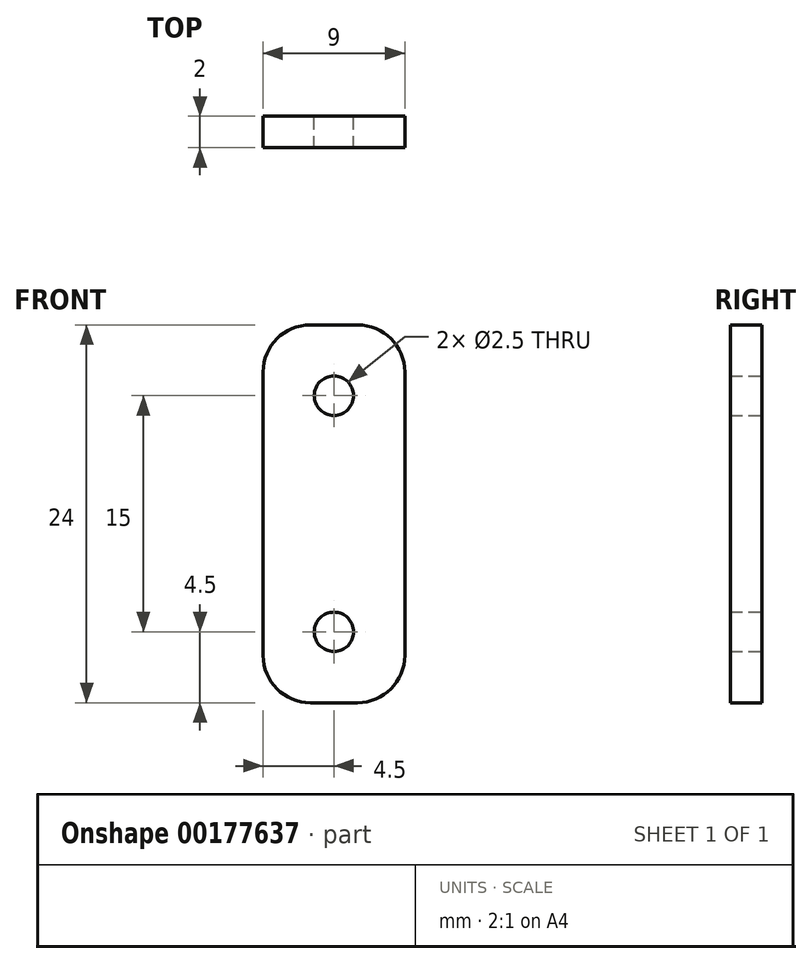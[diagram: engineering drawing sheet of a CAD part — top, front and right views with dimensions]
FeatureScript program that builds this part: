
annotation { "Feature Type Name" : "Feature", "Feature Type Description" : "" }
export const myFeature = defineFeature(function(context is Context, id is Id, definition is map)
    precondition{}
    {
        {
            var Q0;
            Q0=qCreatedBy(makeId("Front.planeOp"),FACE);
            var sketch = newSketch(context, id + "F0", { "sketchPlane" : qUnion([Q0])});
            skLineSegment(sketch, "E0.bottom", {"start": v(4.5, 12) * mm, "end": v(-4.5, 12) * mm});
            skLineSegment(sketch, "E0.top", {"start": v(4.5, -12) * mm, "end": v(-4.5, -12) * mm});
            skLineSegment(sketch, "E0.left", {"start": v(4.5, 12) * mm, "end": v(4.5, -12) * mm});
            skLineSegment(sketch, "E0.right", {"start": v(-4.5, 12) * mm, "end": v(-4.5, -12) * mm});
            skPoint(sketch, "E0.middle", {"position": v(0, 0) * mm});
            skCircle(sketch, "E1", {"center": v(0, 7.5) * mm, "radius": 1.25 * mm});
            skCircle(sketch, "E2", {"center": v(0, -7.5) * mm, "radius": 1.25 * mm});
            skSolve(sketch);
        }
        {
            var Q0;
            Q0=qSketchRegion(id+"F0",true);
            extrude(context, id + "F1", {"entities" : qUnion([Q0]), "depth" : 2 * mm});
        }
        {
            var Q0;
            Q0=makeQuery(id+"F1.opExtrude","SWEPT_EDGE",EDGE,{"disambiguationData":[OSD([sQuery(id+"F0.wireOp",EDGE,"E0.bottom"),sQuery(id+"F0.wireOp",EDGE,"E0.left")])]});
            var Q1;
            Q1=makeQuery(id+"F1.opExtrude","SWEPT_EDGE",EDGE,{"disambiguationData":[OSD([sQuery(id+"F0.wireOp",EDGE,"E0.bottom"),sQuery(id+"F0.wireOp",EDGE,"E0.right")])]});
            var Q2;
            Q2=makeQuery(id+"F1.opExtrude","SWEPT_EDGE",EDGE,{"disambiguationData":[OSD([sQuery(id+"F0.wireOp",EDGE,"E0.top"),sQuery(id+"F0.wireOp",EDGE,"E0.left")])]});
            var Q3;
            Q3=makeQuery(id+"F1.opExtrude","SWEPT_EDGE",EDGE,{"disambiguationData":[OSD([sQuery(id+"F0.wireOp",EDGE,"E0.top"),sQuery(id+"F0.wireOp",EDGE,"E0.right")])]});
            fillet(context, id + "F2", {"entities" : qUnion([Q0, Q1, Q2, Q3]), "radius" : 3 * mm, "tangentPropagation" : true, "allowEdgeOverflow" : false});
        }
    });
